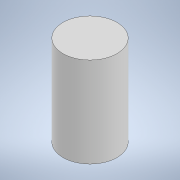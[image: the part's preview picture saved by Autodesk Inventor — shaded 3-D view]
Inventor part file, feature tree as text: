
AUTODESK INVENTOR PART (.ipt)
format: ipt  version: 2020 (Build 240168000, 168)  size: 88,576 bytes
history: native  units: mm
features: extrude x1, sketch x1
ambient origin geometry x8: Origin, YZ Plane, XZ Plane, XY Plane, X Axis, Y Axis, Z Axis, Center Point
bodies: Solid1 (feature_tree)
feature tree (2):
  extrude  "Extrusion1"  Depth=10.0mm TaperAngle=0.0deg
  sketch  "Sketch1"  dims[d0=6.0mm d1=10.0mm d2=0.0mm]
